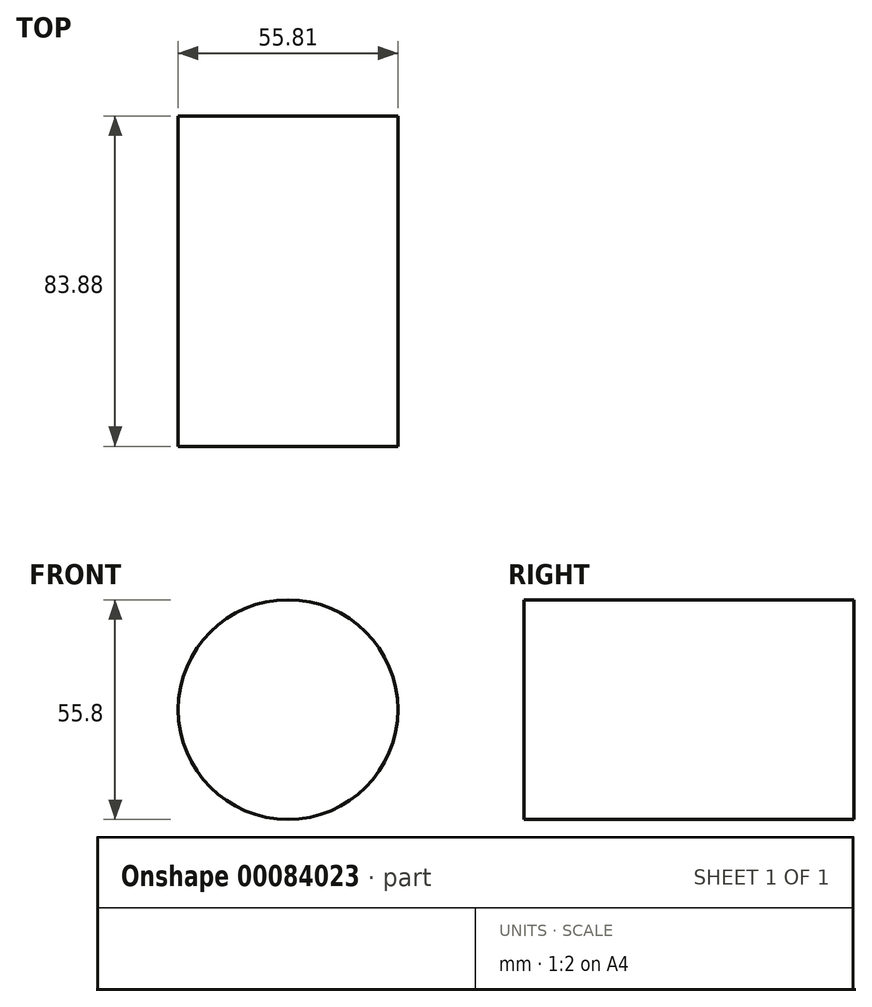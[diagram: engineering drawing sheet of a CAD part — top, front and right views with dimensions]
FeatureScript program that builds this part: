
annotation { "Feature Type Name" : "Feature", "Feature Type Description" : "" }
export const myFeature = defineFeature(function(context is Context, id is Id, definition is map)
    precondition{}
    {
        {
            var Q0;
            Q0=qCreatedBy(makeId("Front.planeOp"),FACE);
            var sketch = newSketch(context, id + "F0", { "sketchPlane" : qUnion([Q0])});
            skCircle(sketch, "E0", {"center": v(34.54, 43.66) * mm, "radius": 27.9 * mm});
            skSolve(sketch);
        }
        {
            var Q0;
            Q0 = qSketchRegion(id + "F0", true);
            extrude(context, id + "F1", {"entities" : qUnion([Q0]), "depth" : 83.88 * mm});
        }
    });
